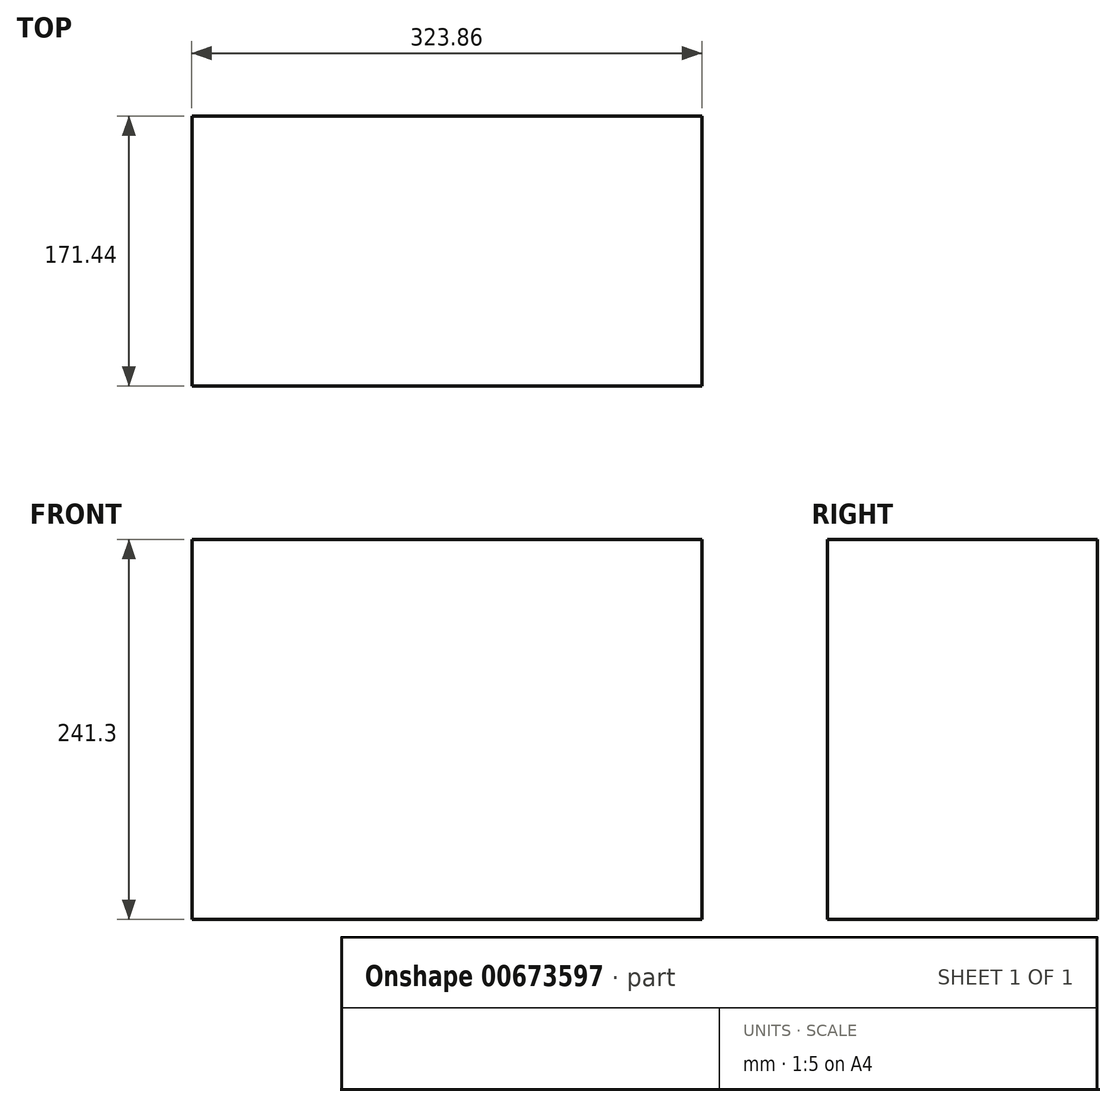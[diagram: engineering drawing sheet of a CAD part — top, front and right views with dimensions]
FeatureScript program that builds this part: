
annotation { "Feature Type Name" : "Feature", "Feature Type Description" : "" }
export const myFeature = defineFeature(function(context is Context, id is Id, definition is map)
    precondition{}
    {
        {
            var Q0;
            Q0=qCreatedBy(makeId("Top.planeOp"),FACE);
            var sketch = newSketch(context, id + "F0", { "sketchPlane" : qUnion([Q0])});
            skLineSegment(sketch, "E0.bottom", {"start": v(-161.93, 85.73) * mm, "end": v(161.93, 85.73) * mm});
            skLineSegment(sketch, "E0.top", {"start": v(-161.93, -85.73) * mm, "end": v(161.92, -85.73) * mm});
            skLineSegment(sketch, "E0.left", {"start": v(-161.93, 85.73) * mm, "end": v(-161.93, -85.73) * mm});
            skLineSegment(sketch, "E0.right", {"start": v(161.93, 85.73) * mm, "end": v(161.92, -85.73) * mm});
            skPoint(sketch, "E0.middle", {"position": v(0, 0) * mm});
            skSolve(sketch);
        }
        {
            var Q0;
            Q0 = qSketchRegion(id + "F0", true);
            extrude(context, id + "F1", {"entities" : qUnion([Q0]), "depth" : 241.3 * mm, "offsetDistance" : 25.4 * mm});
        }
    });
